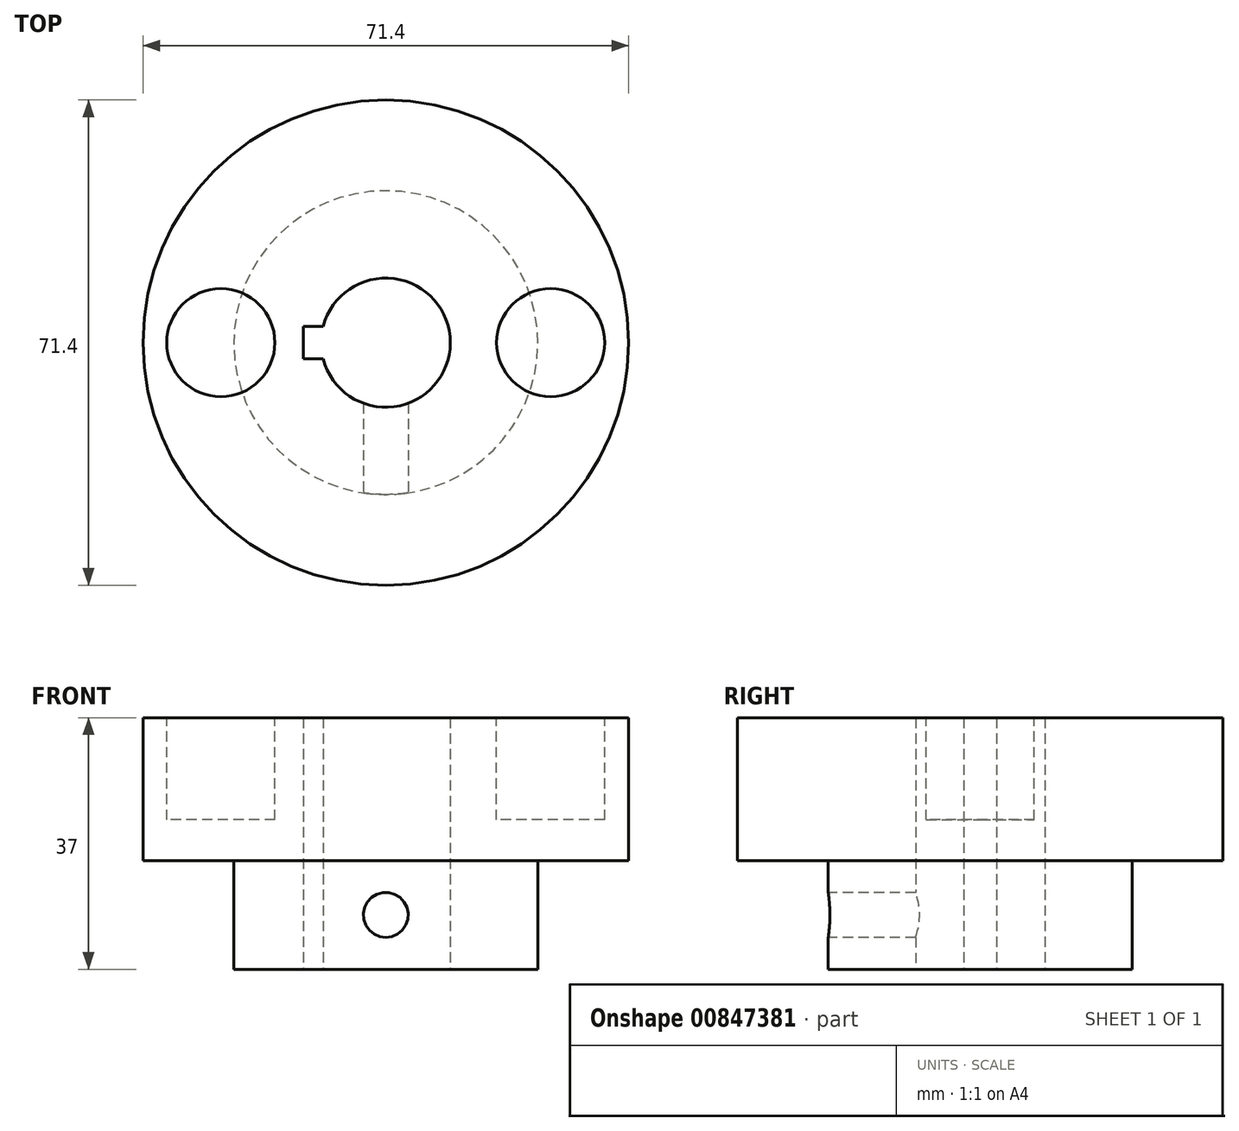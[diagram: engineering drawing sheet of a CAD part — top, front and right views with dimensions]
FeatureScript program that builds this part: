
annotation { "Feature Type Name" : "Feature", "Feature Type Description" : "" }
export const myFeature = defineFeature(function(context is Context, id is Id, definition is map)
    precondition{}
    {
        {
            var Q0;
            Q0=qCreatedBy(makeId("Top.planeOp"),FACE);
            var sketch = newSketch(context, id + "F0", { "sketchPlane" : qUnion([Q0])});
            skCircle(sketch, "E0", {"center": v(0, 0) * mm, "radius": 35.7 * mm});
            skSolve(sketch);
        }
        {
            var Q0;
            Q0=makeQuery(id+"F0.imprint","IMPRINT",FACE,{"disambiguationData":[TD([[makeQuery(id+"F0.imprint","IMPRINT",EDGE,{"derivedFrom":sQuery(id+"F0.wireOp",EDGE,"E0")}),1.0]])]});
            extrude(context, id + "F1", {"entities" : qUnion([Q0]), "depth" : 37 * mm, "offsetDistance" : 25 * mm});
        }
        {
            var Q0;
            Q0=makeQuery(id+"F1.opExtrude","CAP_FACE",FACE,{"disambiguationData":[OSD([sQuery(id+"F0.wireOp",EDGE,"E0")])],"isStart":false});
            var sketch = newSketch(context, id + "F2", { "sketchPlane" : qUnion([Q0])});
            skLineSegment(sketch, "E1", {"start": v(21.05, -28.83) * mm, "end": v(5.2, -13) * mm});
            skPoint(sketch, "E2", {"position": v(0, -35.7) * mm});
            skLineSegment(sketch, "E3", {"start": v(-21.05, -28.83) * mm, "end": v(-5.2, -13) * mm});
            skArc(sketch, "E4", {"start": v(-5.2, -13) * mm, "mid": v(0, -14) * mm, "end": v(5.2, -13) * mm});
            skArc(sketch, "E5", {"start": v(-21.05, -28.83) * mm, "mid": v(0, -35.7) * mm, "end": v(21.05, -28.83) * mm});
            skSolve(sketch);
        }
        {
            var Q0;
            Q0=makeQuery(id+"F1.opExtrude","CAP_FACE",FACE,{"disambiguationData":[OSD([sQuery(id+"F0.wireOp",EDGE,"E0")])],"isStart":true});
            var sketch = newSketch(context, id + "F3", { "sketchPlane" : qUnion([Q0])});
            skCircle(sketch, "E6", {"center": v(0, 0) * mm, "radius": 22.35 * mm});
            skSolve(sketch);
        }
        {
            var Q0;
            Q0=makeQuery(id+"F3.imprint","IMPRINT",FACE,{"disambiguationData":[TD([[makeQuery(id+"F3.imprint","IMPRINT",EDGE,{"derivedFrom":sQuery(id+"F3.wireOp",EDGE,"E6")}),-1.0]])]});
            extrude(context, id + "F4", {"entities" : qUnion([Q0]), "operationType" : NewBodyOperationType.REMOVE, "oppositeDirection" : true, "depth" : 16 * mm, "offsetDistance" : 25 * mm});
        }
        {
            var Q0;
            Q0=makeQuery(id+"F1.opExtrude","CAP_FACE",FACE,{"disambiguationData":[OSD([sQuery(id+"F0.wireOp",EDGE,"E0")])],"isStart":true});
            var sketch = newSketch(context, id + "F5", { "sketchPlane" : qUnion([Q0])});
            skCircle(sketch, "E7", {"center": v(0, 0) * mm, "radius": 9.5 * mm});
            skLineSegment(sketch, "E8.bottom", {"start": v(-12.1, 2.4) * mm, "end": v(0, 2.4) * mm});
            skLineSegment(sketch, "E8.top", {"start": v(-12.1, -2.4) * mm, "end": v(0, -2.4) * mm});
            skLineSegment(sketch, "E8.left", {"start": v(-12.1, 2.4) * mm, "end": v(-12.1, -2.4) * mm});
            skLineSegment(sketch, "E8.right", {"start": v(0, 2.4) * mm, "end": v(0, -2.4) * mm});
            skPoint(sketch, "E8.middle", {"position": v(-6.05, 0) * mm});
            skPoint(sketch, "E9", {"position": v(9.5, 0) * mm});
            skSolve(sketch);
        }
        {
            var Q0;
            {var subQ5=sQuery(id+"F5.wireOp",EDGE,"E8.left");Q0=makeQuery(id+"F5.imprint","IMPRINT",FACE,{"disambiguationData":[TD([[makeQuery(id+"F5.imprint","IMPRINT",EDGE,{"derivedFrom":subQ5}),1.0]])]});}
            var Q1;
            {var subQ5=sQuery(id+"F5.wireOp",EDGE,"E8.right");Q1=makeQuery(id+"F5.imprint","IMPRINT",FACE,{"disambiguationData":[TD([[makeQuery(id+"F5.imprint","IMPRINT",EDGE,{"derivedFrom":subQ5}),-1.0]])]});}
            var Q2;
            {var subQ5=sQuery(id+"F5.wireOp",EDGE,"E8.right");Q2=makeQuery(id+"F5.imprint","IMPRINT",FACE,{"disambiguationData":[TD([[makeQuery(id+"F5.imprint","IMPRINT",EDGE,{"derivedFrom":subQ5}),1.0]])]});}
            extrude(context, id + "F6", {"entities" : qUnion([Q0, Q1, Q2]), "operationType" : NewBodyOperationType.REMOVE, "endBound" : BoundingType.THROUGH_ALL, "oppositeDirection" : true, "depth" : 25 * mm, "offsetDistance" : 25 * mm});
        }
        {
            var Q0;
            Q0=makeQuery(id+"F1.opExtrude","CAP_FACE",FACE,{"disambiguationData":[OSD([sQuery(id+"F0.wireOp",EDGE,"E0")])],"isStart":false});
            var sketch = newSketch(context, id + "F7", { "sketchPlane" : qUnion([Q0])});
            skLineSegment(sketch, "E10", {"start": v(-24.25, 0) * mm, "end": v(24.25, 0) * mm, "construction": true});
            skCircle(sketch, "E11", {"center": v(-24.25, 0) * mm, "radius": 7.95 * mm});
            skCircle(sketch, "E12", {"center": v(24.25, 0) * mm, "radius": 7.95 * mm});
            skSolve(sketch);
        }
        {
            var Q0;
            Q0=makeQuery(id+"F7.imprint","IMPRINT",FACE,{"disambiguationData":[TD([[makeQuery(id+"F7.imprint","IMPRINT",EDGE,{"derivedFrom":sQuery(id+"F7.wireOp",EDGE,"E11")}),1.0]])]});
            var Q1;
            Q1=makeQuery(id+"F7.imprint","IMPRINT",FACE,{"disambiguationData":[TD([[makeQuery(id+"F7.imprint","IMPRINT",EDGE,{"derivedFrom":sQuery(id+"F7.wireOp",EDGE,"E12")}),1.0]])]});
            extrude(context, id + "F8", {"entities" : qUnion([Q0, Q1]), "operationType" : NewBodyOperationType.REMOVE, "oppositeDirection" : true, "depth" : 15 * mm, "offsetDistance" : 25 * mm});
        }
        {
            var Q0;
            Q0=sQuery(id+"F2.wireOp",EDGE,"E5");
            cPoint(context, id + "F9", {"entities" : qUnion([Q0]), "parameter" : 0.5});
        }
        {
            var Q0;
            Q0=qCreatedBy(makeId("Front.planeOp"),FACE);
            var Q1;
            Q1 = qCreatedBy(id + "F9" ,VERTEX);
            cPlane(context, id + "F10", {"entities" : qUnion([Q0, Q1]), "cplaneType" : CPlaneType.PLANE_POINT, "offset" : 25 * mm, "width" : 150 * mm, "height" : 150 * mm});
        }
        {
            var Q0;
            Q0=qCreatedBy(id+"F10.planeOp",FACE);
            var sketch = newSketch(context, id + "F11", { "sketchPlane" : qUnion([Q0])});
            skLineSegment(sketch, "E13.0.0", {"start": v(35.7, 16) * mm, "end": v(-35.7, 16) * mm});
            skPoint(sketch, "E14", {"position": v(0, 8) * mm});
            skPoint(sketch, "E14.positionSnap0", {"position": v(0, 16) * mm});
            skSolve(sketch);
        }
        {
            var Q0;
            Q0=sQuery(id+"F11.wireOp",VERTEX,"E14");
            var Q1;
            Q1=makeQuery(id+"F1.opExtrude","SWEPT_BODY",BODY,{"disambiguationData":[OSD([sQuery(id+"F0.wireOp",EDGE,"E0")])]});
            hole(context, id + "F12", {"style" : HoleStyle.SIMPLE, "endStyle" : HoleEndStyle.BLIND, "standardTappedOrClearance" : lookupTablePath({ "fit" : "Normal", "standard" : "ISO", "size" : "M6", "type" : "Clearance" }), "standardBlindInLast" : lookupTablePath({ "fit" : "Standard", "standard" : "ISO", "size" : "M6", "type" : "Clearance" }), "holeDiameter" : 6.6 * mm, "majorDiameter" : 5 * mm, "holeDepth" : (71.4 / 2) * mm, "isTappedThrough" : true, "tappedDepth" : 12 * mm, "tapClearance" : 3, "startFromSketch" : true, "locations" : qUnion([Q0]), "scope" : qUnion([Q1])});
        }
    });
